# Revit family: Drinking_Fountain-Murdock-GRE2X_Series
name_source: partatom
category: Plumbing Fixtures
units: mm (PartAtom-declared; Revit-internal decimal feet)

## family parameters
Cut with Voids When Loaded = No
Host = Face
OmniClass Number = 23.65.70.14.11
OmniClass Title = Drinking Fountains/Coolers
Part Type = Normal
Room Calculation Point = No
Round Connector Dimension = Use Diameter
Shared = Yes

## types (8) — shared parameters
316 - Type 316 Stainless Steel Construction = No
ADA Compliant = Yes
Assembly Code = D2010800
CW Connection = Yes
CWFU = 1.5
Cold Water Connection Diameter = 3/8"
Cold Water Connection Height = 29 1/2"
Default Elevation = 0"
Description = Barrier-Free, Wall Mounted, Angled Bi-Level Drinking Fountain
FRA3 - Freeze Resistant Valve, Three Valves (Less Filter & Sensor) = No
Finish - Bowl = Metal-Murdock-18_Gauge-304_Stainless_Steel-Satin
Finish - Bubbler = Metal-Murdock-18_Gauge-304_Stainless_Steel-Satin
Flow Rate = 1.0 GPM
HW Connection = No
Height = 38 1/2"
IAPMO Compliance = Fountain shall comply with ANSIA117.1,PublicLaw111-380(NO-LEAD), CHSC 116875 and NSF/ANSI 61, Section 9.
Installation Instruction Link = https://www.murdockmfg.com
Installation Type = Wall Mounted
LOGO - Customer specified logo = No
Manufacturer = Murdock Mfg
PT 1-1/4” OD P-Trap (Access Below Fixture) = No
Pressure Range = 30 to 100 psi
Price = Prices may vary. Please consult Manufacturer Representative for most up-to-date price list.
Product Documentation Link = https://www.murdockmfg.com
Product Page URL = https://www.murdockmfg.com
Revised Date = 04/27/2022
SK8 Stainless Steel Skirt for Upper Unit = No
SO - Sensor Operated Bottle Filler - Battery Operated1Standard (N/A with -FRA2) = No
SOC - Concealed Sensor Operation DrinkingFountain - Battery Operated Standard (N/A with -FRA2) = No
Thickness- Steel Mounting Plate = 1/4"
URL = https://www.murdockmfg.com
Vent Connection = No
Void Edges = 1/4"
WFU = 2
Waste Connection = Yes
Waste Connection Diameter = 1 1/4"
Waste Connection Height = 27 1/2"
Water Pressure = 20-105 PSIG
Width = 34 7/8"
zero-valued in all types: HWFU

## per-type parameters (varying)
| type | Finish | L- ADA Drinking Fountain Left Side | Material | R- ADA Drinking Fountain Right Side | Station Hegiht- Right | Station Height- Left |
| GRE25-L | Metal-Murdock-12_Gauge-Stainless_Steel-Green_Powder_Coated | Yes | Metal-Murdock-12_Gauge-Stainless_Steel-Green_Powder_Coated | No | 27" | 32 3/8" |
| GRE25-R | Metal-Murdock-12_Gauge-Stainless_Steel-Green_Powder_Coated | No | Metal-Murdock-12_Gauge-Stainless_Steel-Green_Powder_Coated | Yes | 32 3/8" | 27" |
| GRE24-L | Metal-Murdock-12 Gauge-Stainless_Steel-Satin | Yes | Metal-Murdock-12 Gauge-Stainless_Steel-Satin | No | 27" | 32 3/8" |
| GRE24-R | Metal-Murdock-12 Gauge-Stainless_Steel-Satin | No | Metal-Murdock-12 Gauge-Stainless_Steel-Satin | Yes | 32 3/8" | 27" |
| GRE26-R | Metal-Murdock-12_Gauge-Stainless_Steel-Red_Powder_Coated | No | Metal-Murdock-12_Gauge-Stainless_Steel-Red_Powder_Coated | Yes | 32 3/8" | 27" |
| GRE26-L | Metal-Murdock-12_Gauge-Stainless_Steel-Red_Powder_Coated | Yes | Metal-Murdock-12_Gauge-Stainless_Steel-Red_Powder_Coated | No | 27" | 32 3/8" |
| GRE27-L | Metal-Murdock-12_Gauge-Stainless_Steel-Blue_Powder_Coated | Yes | Metal-Murdock-12_Gauge-Stainless_Steel-Blue_Powder_Coated | No | 27" | 32 3/8" |
| GRE27-R | Metal-Murdock-12_Gauge-Stainless_Steel-Blue_Powder_Coated | No | Metal-Murdock-12_Gauge-Stainless_Steel-Blue_Powder_Coated | Yes | 32 3/8" | 27" |

note: column(s) folded — value = type name in every type: Model

## geometry (parser evidence)
native form markers: Sweep x2
no freeform markers — native parametric forms only
